# Revit family: Practibox_S_surface_mounting_cabinet_22_modules_réf_137105_to_137215
name_source: partatom
category: Equipement électrique
revit_build: Autodesk Revit 2018 (Build: 20170223_1515(x64)
units: mm (PartAtom-declared; Revit-internal decimal feet)

## family parameters
Basée sur le plan de construction = Non
Configuration du panneau = Deux colonnes, circuits au sein
Cote de connecteur circulaire = Utiliser le diamètre
Couper avec des vides une fois chargée = Non
Numéro OmniClass = 23.80.30.11.17
Partagée = Non
Point de calcul de pièce = Non
Titre OmniClass = Distribution Boards and Control Panels
Toujours verticalement = Oui
Type d'élément = Tableau de raccordement

## types (4) — shared parameters
Fabricant = "Legrand"
General Conditions of Use = https://export.legrand.com
Ina = 90A
URL = www.legrand.com
depth = 390 mm  [stored 1.27953 ft]
height = 236 mm
size = 22 modules
width = 508 mm

## per-type parameters (varying)
| type | Terminal block E | Terminal block N | door transparent | door white |
| Practibox_S_surface_mounting_cabinet_22_modules_137105 |  |  | Non | Oui |
| Practibox_S_surface_mounting_cabinet_22_modules_137115 |  |  | Oui | Non |
| Practibox_S_surface_mounting_cabinet_22_modules_137205 | 13 connections Icc 10kA | 13 connections Icc 10kA | Non | Oui |
| Practibox_S_surface_mounting_cabinet_22_modules_137215 | 13 connections Icc 10kA | 13 connections Icc 10kA | Oui | Non |

note: column(s) folded — value = type name in every type: Description

note: [stored X ft] marks values corroborated as IEEE doubles in the binary element streams (Revit-internal decimal feet)
